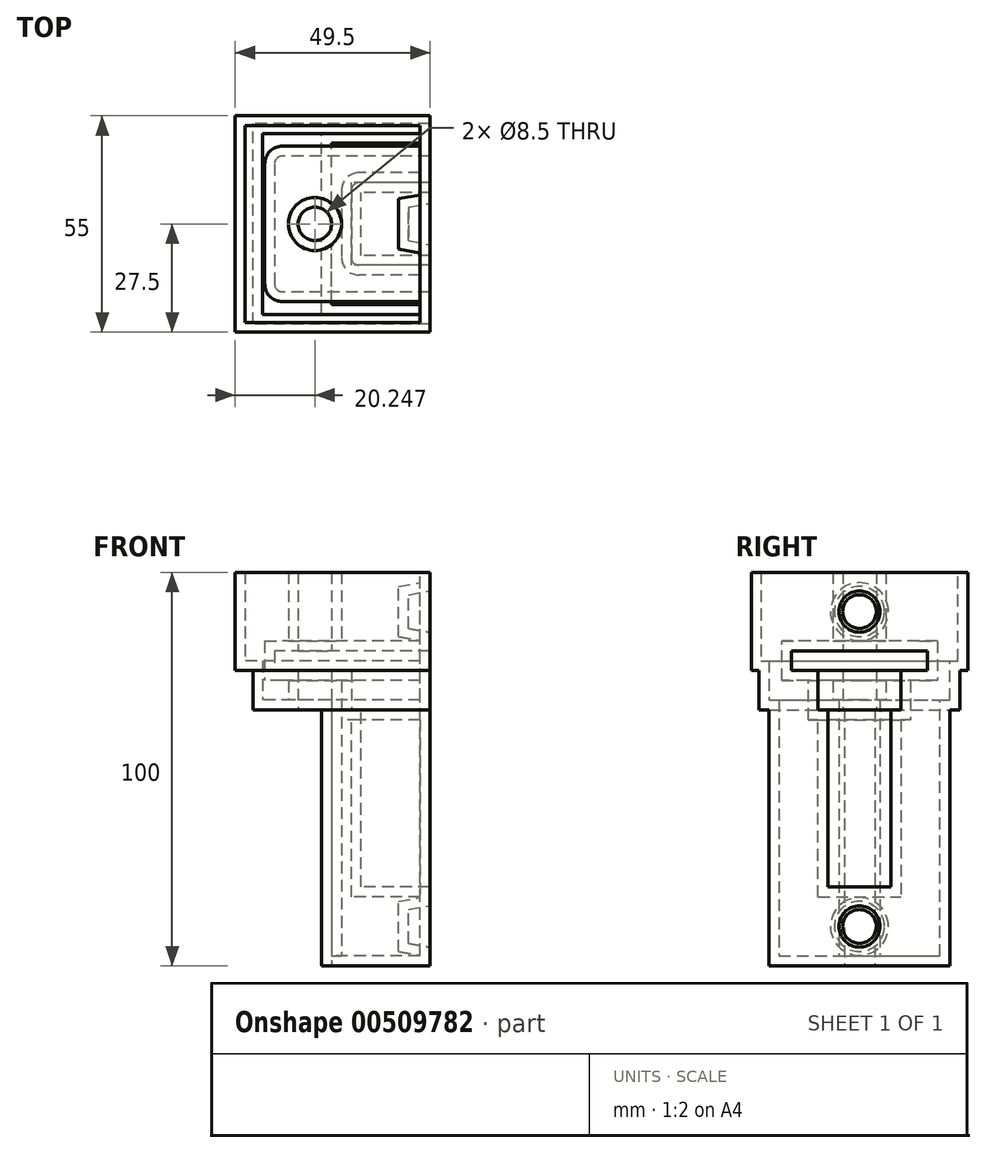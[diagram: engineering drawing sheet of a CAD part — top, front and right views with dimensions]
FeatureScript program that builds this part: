
annotation { "Feature Type Name" : "Feature", "Feature Type Description" : "" }
export const myFeature = defineFeature(function(context is Context, id is Id, definition is map)
    precondition{}
    {
        {
            var Q0;
            Q0=qCreatedBy(makeId("Top.planeOp"),FACE);
            var sketch = newSketch(context, id + "F0", { "sketchPlane" : qUnion([Q0])});
            skLineSegment(sketch, "E0.bottom", {"start": v(27.5, -23) * mm, "end": v(-27.5, -23) * mm});
            skLineSegment(sketch, "E0.top", {"start": v(27.5, 23) * mm, "end": v(-27.5, 23) * mm});
            skLineSegment(sketch, "E0.left", {"start": v(27.5, -23) * mm, "end": v(27.5, 23) * mm});
            skLineSegment(sketch, "E0.right", {"start": v(-27.5, -23) * mm, "end": v(-27.5, 23) * mm});
            skPoint(sketch, "E0.middle", {"position": v(0, 0) * mm});
            skSolve(sketch);
        }
        {
            var Q0;
            Q0 = qSketchRegion(id + "F0", true);
            extrude(context, id + "F1", {"entities" : qUnion([Q0]), "depth" : 65 * mm});
        }
        {
            var Q0;
            Q0=makeQuery(id+"F1.opExtrude","CAP_FACE",FACE,{"disambiguationData":[OSD([sQuery(id+"F0.wireOp",EDGE,"E0.bottom"),sQuery(id+"F0.wireOp",EDGE,"E0.top"),sQuery(id+"F0.wireOp",EDGE,"E0.left"),sQuery(id+"F0.wireOp",EDGE,"E0.right")])],"isStart":false});
            var sketch = newSketch(context, id + "F2", { "sketchPlane" : qUnion([Q0])});
            skLineSegment(sketch, "E1.bottom", {"start": v(17.5, -8) * mm, "end": v(-17.5, -8) * mm});
            skLineSegment(sketch, "E1.top", {"start": v(17.5, 8) * mm, "end": v(-17.5, 8) * mm});
            skLineSegment(sketch, "E1.left", {"start": v(17.5, -8) * mm, "end": v(17.5, 8) * mm});
            skLineSegment(sketch, "E1.right", {"start": v(-17.5, -8) * mm, "end": v(-17.5, 8) * mm});
            skPoint(sketch, "E1.middle", {"position": v(0, 0) * mm});
            skSolve(sketch);
        }
        {
            var Q0;
            Q0 = qSketchRegion(id + "F2", true);
            extrude(context, id + "F3", {"entities" : qUnion([Q0]), "operationType" : NewBodyOperationType.REMOVE, "oppositeDirection" : true, "depth" : 45 * mm});
        }
        {
            var Q0;
            Q0=makeQuery(id+"F1.opExtrude","CAP_FACE",FACE,{"disambiguationData":[OSD([sQuery(id+"F0.wireOp",EDGE,"E0.bottom"),sQuery(id+"F0.wireOp",EDGE,"E0.top"),sQuery(id+"F0.wireOp",EDGE,"E0.left"),sQuery(id+"F0.wireOp",EDGE,"E0.right")])],"isStart":false});
            var sketch = newSketch(context, id + "F4", { "sketchPlane" : qUnion([Q0])});
            skLineSegment(sketch, "E2.bottom", {"start": v(45, -25.5) * mm, "end": v(-45, -25.5) * mm});
            skLineSegment(sketch, "E2.top", {"start": v(45, 25.5) * mm, "end": v(-45, 25.5) * mm});
            skLineSegment(sketch, "E2.left", {"start": v(45, -25.5) * mm, "end": v(45, 25.5) * mm});
            skLineSegment(sketch, "E2.right", {"start": v(-45, -25.5) * mm, "end": v(-45, 25.5) * mm});
            skPoint(sketch, "E2.middle", {"position": v(0, 0) * mm});
            skSolve(sketch);
        }
        {
            var Q0;
            Q0 = qSketchRegion(id + "F4", true);
            extrude(context, id + "F5", {"entities" : qUnion([Q0]), "operationType" : NewBodyOperationType.ADD, "depth" : 10 * mm});
        }
        {
            var Q0;
            {var subQ0=sQuery(id+"F4.wireOp",EDGE,"E2.right");var subQ1=sQuery(id+"F4.wireOp",EDGE,"E2.bottom");var subQ2=sQuery(id+"F4.wireOp",EDGE,"E2.top");var subQ3=sQuery(id+"F4.wireOp",EDGE,"E2.left");Q0=makeQuery(id+"F5.boolean.opBoolean","SPLIT",FACE,{"disambiguationData":[TD([makeQuery(id+"F1.opExtrude","SWEPT_FACE",FACE,{"disambiguationData":[OSD([sQuery(id+"F0.wireOp",EDGE,"E0.bottom")])]})])],"derivedFrom":makeQuery(id+"F5.opExtrude","CAP_FACE",FACE,{"disambiguationData":[OSD([subQ1,subQ2,subQ3,subQ0])],"isStart":true})});}
            var sketch = newSketch(context, id + "F6", { "sketchPlane" : qUnion([Q0])});
            skLineSegment(sketch, "E3.bottom", {"start": v(20, -10.5) * mm, "end": v(-20, -10.5) * mm});
            skLineSegment(sketch, "E3.top", {"start": v(20, 10.5) * mm, "end": v(-20, 10.5) * mm});
            skLineSegment(sketch, "E3.left", {"start": v(20, -10.5) * mm, "end": v(20, 10.5) * mm});
            skLineSegment(sketch, "E3.right", {"start": v(-20, -10.5) * mm, "end": v(-20, 10.5) * mm});
            skPoint(sketch, "E3.middle", {"position": v(0, 0) * mm});
            skSolve(sketch);
        }
        {
            var Q0;
            Q0 = qSketchRegion(id + "F6", true);
            extrude(context, id + "F7", {"entities" : qUnion([Q0]), "operationType" : NewBodyOperationType.REMOVE, "oppositeDirection" : true, "depth" : 10 * mm});
        }
        {
            var Q0;
            Q0=makeQuery(id+"F7.boolean.opBoolean","COPY",EDGE,{"derivedFrom":makeQuery(id+"F7.opExtrude","SWEPT_EDGE",EDGE,{"disambiguationData":[OSD([sQuery(id+"F6.wireOp",EDGE,"E3.top"),sQuery(id+"F6.wireOp",EDGE,"E3.right")])]})});
            var Q1;
            Q1=makeQuery(id+"F7.boolean.opBoolean","COPY",EDGE,{"derivedFrom":makeQuery(id+"F7.opExtrude","SWEPT_EDGE",EDGE,{"disambiguationData":[OSD([sQuery(id+"F6.wireOp",EDGE,"E3.bottom"),sQuery(id+"F6.wireOp",EDGE,"E3.right")])]})});
            var Q2;
            Q2=makeQuery(id+"F7.boolean.opBoolean","COPY",EDGE,{"derivedFrom":makeQuery(id+"F7.opExtrude","SWEPT_EDGE",EDGE,{"disambiguationData":[OSD([sQuery(id+"F6.wireOp",EDGE,"E3.bottom"),sQuery(id+"F6.wireOp",EDGE,"E3.left")])]})});
            var Q3;
            Q3=makeQuery(id+"F7.boolean.opBoolean","COPY",EDGE,{"derivedFrom":makeQuery(id+"F7.opExtrude","SWEPT_EDGE",EDGE,{"disambiguationData":[OSD([sQuery(id+"F6.wireOp",EDGE,"E3.top"),sQuery(id+"F6.wireOp",EDGE,"E3.left")])]})});
            fillet(context, id + "F8", {"entities" : qUnion([Q0, Q1, Q2, Q3]), "radius" : 2 * mm, "tangentPropagation" : true, "allowEdgeOverflow" : false});
        }
        {
            var Q0;
            Q0=makeQuery(id+"F5.opExtrude","CAP_FACE",FACE,{"disambiguationData":[OSD([sQuery(id+"F4.wireOp",EDGE,"E2.bottom"),sQuery(id+"F4.wireOp",EDGE,"E2.top"),sQuery(id+"F4.wireOp",EDGE,"E2.left"),sQuery(id+"F4.wireOp",EDGE,"E2.right")])],"isStart":false});
            var sketch = newSketch(context, id + "F9", { "sketchPlane" : qUnion([Q0])});
            skLineSegment(sketch, "E4.bottom", {"start": v(49.5, -27.5) * mm, "end": v(-49.5, -27.5) * mm});
            skLineSegment(sketch, "E4.top", {"start": v(49.5, 27.5) * mm, "end": v(-49.5, 27.5) * mm});
            skLineSegment(sketch, "E4.left", {"start": v(49.5, -27.5) * mm, "end": v(49.5, 27.5) * mm});
            skLineSegment(sketch, "E4.right", {"start": v(-49.5, -27.5) * mm, "end": v(-49.5, 27.5) * mm});
            skPoint(sketch, "E4.middle", {"position": v(0, 0) * mm});
            skSolve(sketch);
        }
        {
            var Q0;
            Q0 = qSketchRegion(id + "F9", true);
            extrude(context, id + "F10", {"entities" : qUnion([Q0]), "operationType" : NewBodyOperationType.ADD, "depth" : 25 * mm});
        }
        {
            var Q0;
            {var subQ0=sQuery(id+"F9.wireOp",EDGE,"E4.bottom");var subQ1=sQuery(id+"F9.wireOp",EDGE,"E4.top");var subQ2=sQuery(id+"F9.wireOp",EDGE,"E4.left");var subQ3=sQuery(id+"F9.wireOp",EDGE,"E4.right");Q0=makeQuery(id+"F10.boolean.opBoolean","SPLIT",FACE,{"disambiguationData":[TD([makeQuery(id+"F5.opExtrude","SWEPT_FACE",FACE,{"disambiguationData":[OSD([sQuery(id+"F4.wireOp",EDGE,"E2.bottom")])]})])],"derivedFrom":makeQuery(id+"F10.opExtrude","CAP_FACE",FACE,{"disambiguationData":[OSD([subQ0,subQ1,subQ2,subQ3])],"isStart":true})});}
            var sketch = newSketch(context, id + "F11", { "sketchPlane" : qUnion([Q0])});
            skLineSegment(sketch, "E5.bottom", {"start": v(39.5, -17.25) * mm, "end": v(-39.5, -17.25) * mm});
            skLineSegment(sketch, "E5.top", {"start": v(39.5, 17.25) * mm, "end": v(-39.5, 17.25) * mm});
            skLineSegment(sketch, "E5.left", {"start": v(39.5, -17.25) * mm, "end": v(39.5, 17.25) * mm});
            skLineSegment(sketch, "E5.right", {"start": v(-39.5, -17.25) * mm, "end": v(-39.5, 17.25) * mm});
            skPoint(sketch, "E5.middle", {"position": v(0, 0) * mm});
            skLineSegment(sketch, "E6.bottom", {"start": v(-27.93, -52.48) * mm, "end": v(-110.22, -52.48) * mm});
            skLineSegment(sketch, "E6.top", {"start": v(-27.93, -53.94) * mm, "end": v(-110.22, -53.94) * mm});
            skLineSegment(sketch, "E6.left", {"start": v(-27.93, -52.48) * mm, "end": v(-27.93, -53.94) * mm});
            skLineSegment(sketch, "E6.right", {"start": v(-110.22, -52.48) * mm, "end": v(-110.22, -53.94) * mm});
            skPoint(sketch, "E6.middle", {"position": v(-69.08, -53.2) * mm});
            skSolve(sketch);
        }
        {
            var Q0;
            Q0 = qSketchRegion(id + "F11", true);
            extrude(context, id + "F12", {"entities" : qUnion([Q0]), "operationType" : NewBodyOperationType.REMOVE, "oppositeDirection" : true, "depth" : 5 * mm});
        }
        {
            var Q0;
            Q0=makeQuery(id+"F12.boolean.opBoolean","COPY",EDGE,{"derivedFrom":makeQuery(id+"F12.opExtrude","SWEPT_EDGE",EDGE,{"disambiguationData":[OSD([sQuery(id+"F11.wireOp",EDGE,"E5.bottom"),sQuery(id+"F11.wireOp",EDGE,"E5.right")])]})});
            fillet(context, id + "F13", {"entities" : qUnion([Q0]), "radius" : 2 * mm, "tangentPropagation" : true, "allowEdgeOverflow" : false});
        }
        {
            var Q0;
            Q0=makeQuery(id+"F12.boolean.opBoolean","COPY",EDGE,{"derivedFrom":makeQuery(id+"F12.opExtrude","SWEPT_EDGE",EDGE,{"disambiguationData":[OSD([sQuery(id+"F11.wireOp",EDGE,"E5.top"),sQuery(id+"F11.wireOp",EDGE,"E5.right")])]})});
            fillet(context, id + "F14", {"entities" : qUnion([Q0]), "radius" : 2 * mm, "tangentPropagation" : true, "allowEdgeOverflow" : false});
        }
        {
            var Q0;
            Q0=makeQuery(id+"F12.boolean.opBoolean","COPY",EDGE,{"derivedFrom":makeQuery(id+"F12.opExtrude","SWEPT_EDGE",EDGE,{"disambiguationData":[OSD([sQuery(id+"F11.wireOp",EDGE,"E5.top"),sQuery(id+"F11.wireOp",EDGE,"E5.left")])]})});
            fillet(context, id + "F15", {"entities" : qUnion([Q0]), "radius" : 2 * mm, "tangentPropagation" : true, "allowEdgeOverflow" : false});
        }
        {
            var Q0;
            Q0=makeQuery(id+"F12.boolean.opBoolean","COPY",EDGE,{"derivedFrom":makeQuery(id+"F12.opExtrude","SWEPT_EDGE",EDGE,{"disambiguationData":[OSD([sQuery(id+"F11.wireOp",EDGE,"E5.bottom"),sQuery(id+"F11.wireOp",EDGE,"E5.left")])]})});
            fillet(context, id + "F16", {"entities" : qUnion([Q0]), "radius" : 2 * mm, "tangentPropagation" : true, "allowEdgeOverflow" : false});
        }
        {
            var Q0;
            Q0=makeQuery(id+"F12.boolean.opBoolean","COPY",FACE,{"derivedFrom":makeQuery(id+"F12.opExtrude","CAP_FACE",FACE,{"disambiguationData":[OSD([sQuery(id+"F11.wireOp",EDGE,"E5.bottom"),sQuery(id+"F11.wireOp",EDGE,"E5.top"),sQuery(id+"F11.wireOp",EDGE,"E5.left"),sQuery(id+"F11.wireOp",EDGE,"E5.right")])],"isStart":false})});
            var sketch = newSketch(context, id + "F17", { "sketchPlane" : qUnion([Q0])});
            skLineSegment(sketch, "E7", {"start": v(-39.25, -0.06) * mm, "end": v(-29.25, 0) * mm});
            skCircle(sketch, "E8", {"center": v(-29.25, 0) * mm, "radius": 4.25 * mm});
            skSolve(sketch);
        }
        {
            var Q0;
            Q0 = qSketchRegion(id + "F17", true);
            extrude(context, id + "F18", {"entities" : qUnion([Q0]), "operationType" : NewBodyOperationType.REMOVE, "endBound" : BoundingType.SYMMETRIC, "oppositeDirection" : true, "depth" : 200 * mm});
        }
        {
            var Q0;
            Q0=makeQuery(id+"F12.boolean.opBoolean","COPY",FACE,{"derivedFrom":makeQuery(id+"F12.opExtrude","CAP_FACE",FACE,{"disambiguationData":[OSD([sQuery(id+"F11.wireOp",EDGE,"E5.bottom"),sQuery(id+"F11.wireOp",EDGE,"E5.top"),sQuery(id+"F11.wireOp",EDGE,"E5.left"),sQuery(id+"F11.wireOp",EDGE,"E5.right")])],"isStart":false})});
            var sketch = newSketch(context, id + "F19", { "sketchPlane" : qUnion([Q0])});
            skLineSegment(sketch, "E9", {"start": v(39.5, 0) * mm, "end": v(29.5, 0) * mm});
            skPoint(sketch, "E9.endSnap0", {"position": v(39.5, 0) * mm});
            skCircle(sketch, "E10", {"center": v(29.5, 0) * mm, "radius": 4.25 * mm});
            skSolve(sketch);
        }
        {
            var Q0;
            Q0 = qSketchRegion(id + "F19", true);
            extrude(context, id + "F20", {"entities" : qUnion([Q0]), "operationType" : NewBodyOperationType.ADD, "depth" : 5 * mm});
        }
        {
            var Q0;
            Q0=qCreatedBy(makeId("Right.planeOp"),FACE);
            var sketch = newSketch(context, id + "F21", { "sketchPlane" : qUnion([Q0])});
            skLineSegment(sketch, "E11.bottom", {"start": v(-77.03, 103.08) * mm, "end": v(67.56, 103.08) * mm});
            skLineSegment(sketch, "E11.top", {"start": v(-77.03, -60.44) * mm, "end": v(67.56, -60.44) * mm});
            skLineSegment(sketch, "E11.left", {"start": v(-77.03, 103.08) * mm, "end": v(-77.03, -60.44) * mm});
            skLineSegment(sketch, "E11.right", {"start": v(67.56, 103.08) * mm, "end": v(67.56, -60.44) * mm});
            skSolve(sketch);
        }
        {
            var Q0;
            Q0=makeQuery(id+"F21.imprint","IMPRINT",FACE,{"disambiguationData":[TD([[makeQuery(id+"F21.imprint","IMPRINT",EDGE,{"derivedFrom":sQuery(id+"F21.wireOp",EDGE,"E11.bottom")}),-1.0]])]});
            var Q1;
            Q1=makeQuery(id+"F10.opExtrude","SWEPT_FACE",FACE,{"disambiguationData":[OSD([sQuery(id+"F9.wireOp",EDGE,"E4.left")])]});
            var Q2;
            Q2=makeQuery(id+"F1.opExtrude","SWEPT_FACE",FACE,{"disambiguationData":[OSD([sQuery(id+"F0.wireOp",EDGE,"E0.left")])]});
            extrude(context, id + "F22", {"entities" : qUnion([Q0, Q1, Q2]), "operationType" : NewBodyOperationType.REMOVE, "endBound" : BoundingType.THROUGH_ALL, "depth" : 25 * mm});
        }
        {
            var Q0;
            Q0=makeQuery(id+"F22.boolean.opBoolean","COPY",FACE,{"derivedFrom":makeQuery(id+"F22.opExtrude","CAP_FACE",FACE,{"disambiguationData":[OSD([sQuery(id+"F21.wireOp",EDGE,"E11.bottom"),sQuery(id+"F21.wireOp",EDGE,"E11.top"),sQuery(id+"F21.wireOp",EDGE,"E11.left"),sQuery(id+"F21.wireOp",EDGE,"E11.right")])],"isStart":true})});
            var sketch = newSketch(context, id + "F23", { "sketchPlane" : qUnion([Q0])});
            skCircle(sketch, "E12", {"center": v(0, 10) * mm, "radius": 5.25 * mm});
            skCircle(sketch, "E13", {"center": v(0, 90) * mm, "radius": 5.25 * mm});
            skPoint(sketch, "E13.centerSnap0", {"position": v(0, 100) * mm});
            skSolve(sketch);
        }
        {
            var Q0;
            Q0 = qSketchRegion(id + "F23", true);
            extrude(context, id + "F24", {"entities" : qUnion([Q0]), "operationType" : NewBodyOperationType.REMOVE, "oppositeDirection" : true, "depth" : 5.5 * mm, "hasDraft" : true, "draftAngle" : 10 * degree, "draftPullDirection" : true});
        }
        {
            var Q0;
            Q0=makeQuery(id+"F10.opExtrude","CAP_FACE",FACE,{"disambiguationData":[OSD([sQuery(id+"F9.wireOp",EDGE,"E4.bottom"),sQuery(id+"F9.wireOp",EDGE,"E4.top"),sQuery(id+"F9.wireOp",EDGE,"E4.left"),sQuery(id+"F9.wireOp",EDGE,"E4.right")])],"isStart":false});
            shell(context, id + "F25", {"entities" : qUnion([Q0]), "thickness" : 2.5 * mm});
        }
    });
